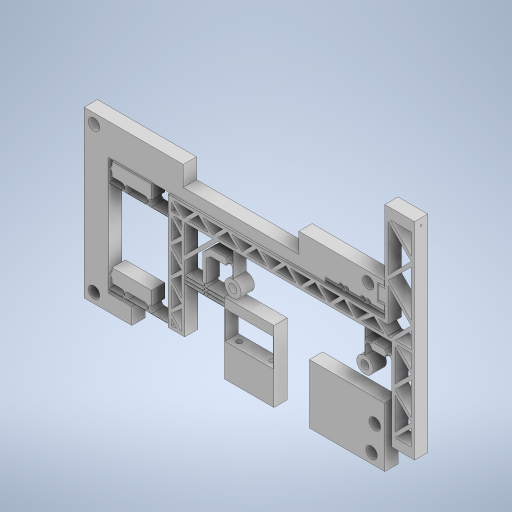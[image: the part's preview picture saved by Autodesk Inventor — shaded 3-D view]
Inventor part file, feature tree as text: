
AUTODESK INVENTOR PART (.ipt)
format: ipt  version: 2023 (Build 270158000, 158)  size: 1,038,848 bytes
history: native  units: mm
features: extrude x12, sketch x11, reference x11, other x6, projected_geometry x2
ambient origin geometry x8: Origin, YZ Plane, XZ Plane, XY Plane, X Axis, Y Axis, Z Axis, Center Point
bodies: Solid1 (feature_tree)
feature tree (42):
  extrude  "Extrusion1"  Depth=20.0mm
  extrude  "Extrusion2"  Depth=4.0mm TaperAngle=0.0deg
  extrude  "Extrusion3"  Depth=0.5mm
  extrude  "Extrusion4"  Depth=5.0mm
  extrude  "Extrusion5"  Depth=18.0mm
  extrude  "Extrusion7"  Depth=1.0mm
  extrude  "Extrusion8"  Depth=1.0mm
  extrude  "Extrusion9"  Depth=0.1mm
  extrude  "Extrusion10"  Depth=5.0mm
  extrude  "Extrusion11"  Depth=0.1mm
  extrude  "Extrusion13"  Depth=15.0mm
  extrude  "Extrusion12"  Depth=18.0mm
  sketch  "Sketch1"  dims[d0=4.0mm d1=0.0mm d2=20.0mm]
  reference  "Reference1"
  sketch  "Sketch2"  dims[d3=9.0mm d4=4.0mm d5=0.0mm]
  sketch  "Sketch6"  dims[d6=7.0mm d7=0.5mm]
  reference  "Reference2"
  sketch  "Sketch7"  dims[d8=4.0mm d9=0.0mm d27=5.0mm]
  sketch  "Sketch9"  dims[d28=30.0mm d29=18.0mm]
  sketch  "Sketch10"  dims[d30=0.1mm d31=1.0mm]
  sketch  "Sketch11"  dims[d32=0.1mm d33=1.0mm]
  reference  "Reference3"
  reference  "Reference4"
  reference  "Reference5"
  reference  "Reference6"
  reference  "Reference7"
  reference  "Reference8"
  sketch  "Sketch12"  dims[d34=15.0mm d35=0.1mm]
  reference  "Reference9"
  reference  "Reference10"
  reference  "Reference11"
  sketch  "Sketch13"  dims[d37=5.0mm d39=5.0mm]
  sketch  "Sketch14"  dims[d40=0.1mm d41=0.1mm]
  projected_geometry  "Projected Loop1"
  projected_geometry  "Projected Loop2"
  sketch  "Sketch15"  dims[d43=0.0mm d44=15.0mm d45=18.0mm d46=2.0mm d47=0.1mm d48=40.0mm d49=2.4mm d50=2.4mm d51=5.0mm d52=5.0mm d53=0.1mm d54=0.05mm d55=0.05mm d56=0.1mm d57=8.0mm d58=0.1mm d59=2.0mm d60=1.5mm d61=5.0mm d62=0.5mm d63=0.5mm d64=0.1mm d65=0.1mm d66=5.0mm d67=0.0mm d68=0.0mm d69=15.0mm d70=10.0mm d71=15.0mm d72=0.0mm d73=1.5mm d74=1.5mm d75=0.2mm d76=0.2mm d79=1.0mm d80=0.1mm d81=0.1mm d82=1.0mm d83=4.0mm d84=0.0mm d87=15.0mm d88=10.0mm d89=10.0mm d90=10.0mm d91=10.0mm d92=0.1mm d93=0.75mm d94=2.0mm d95=1.5mm d97=18.0mm d98=7.0mm d99=4.0mm d100=0.0mm d105=2.0mm d106=6.9mm d107=20.0mm d108=35.0mm d110=6.0mm d111=4.0mm d112=0.0mm d113=2.0mm d114=2.0mm d115=10.0mm d116=2.5mm d117=1.6mm d118=1.6mm d119=10.0mm d120=0.0mm d121=30.0mm d122=10.0mm d123=0.0mm d124=13.0mm d125=3.0mm d126=3.0mm d127=4.0mm d128=3.4mm d129=3.4mm d130=0.1mm d131=7.0mm d132=5.0mm d133=8.0mm d134=0.0mm d135=12.0mm d140=-1.0mm d141=1.0mm d142=2.0mm d143=2.0mm d144=2.1mm d145=2.0mm d146=2.0mm d147=2.1mm d148=0.0mm d149=1.0mm d150=1.0mm d151=2.0mm d152=2.0mm d153=5.0mm d154=1.6mm d155=5.0mm d156=1.6mm d157=1.0mm d158=1.0mm d159=1.0mm d160=1.0mm d161=1.1mm d162=1.1mm d163=5.45mm d164=5.45mm d165=1.0mm d166=1.0mm d167=5.0mm d168=2.0mm d169=2.1mm d170=2.0mm d171=5.0mm d172=2.1mm d173=2.0mm d174=2.0mm d176=2.0mm d177=2.0mm d178=2.1mm d179=2.0mm d180=2.0mm d181=5.0mm d182=2.1mm d183=5.0mm d184=2.1mm d185=2.0mm d186=2.0mm d187=2.0mm d188=2.0mm d189=2.1mm d190=2.1mm d191=2.9mm d192=2.9mm d193=1.1mm d194=0.0mm d195=2.0mm d196=2.0mm d197=0.51mm d198=20.0mm d199=0.0mm d200=10.0mm d201=0.0mm d202=1.0mm d203=1.0mm d204=1.0mm d205=1.0mm d206=9.0mm d207=45.0deg d208=1.0mm d209=0.5mm d211=1.0mm d212=1.0mm d213=1.0mm d214=1.0mm d215=1.0mm d216=1.0mm d217=1.0mm d219=1.0mm d220=0.5mm d221=45.0deg d222=1.0mm d223=1.0mm d224=1.0mm d225=1.0mm d226=1.0mm d227=1.0mm d228=1.0mm d229=0.5mm d230=45.0deg d231=1.0mm d232=1.0mm d233=1.0mm d234=1.0mm d235=1.0mm d236=1.0mm d237=1.0mm d238=1.0mm d239=1.0mm d240=1.0mm d241=1.0mm d242=1.0mm d243=1.0mm d244=1.0mm d245=1.0mm d246=1.0mm d247=1.0mm d248=1.0mm d249=1.0mm d250=0.5mm d251=1.0mm d252=1.0mm d253=1.0mm d254=1.0mm d255=1.0mm d256=1.0mm d257=1.0mm d258=10.0mm d259=0.0mm d24=0.5mm d25=0.872665mm d26=0.5mm]
  other  "<userpath>\ClawdDrive\Objet3D\IminaProbe\V3Roue\RoueV3.iam"
  other  "RoueV3.iam"
  other  "RoueV3partA:1"
  other  "DifferentialLinearActuator:1"
  other  "RoueV3PartC:1"
  other  "DifferentialLinearActuator:5"
